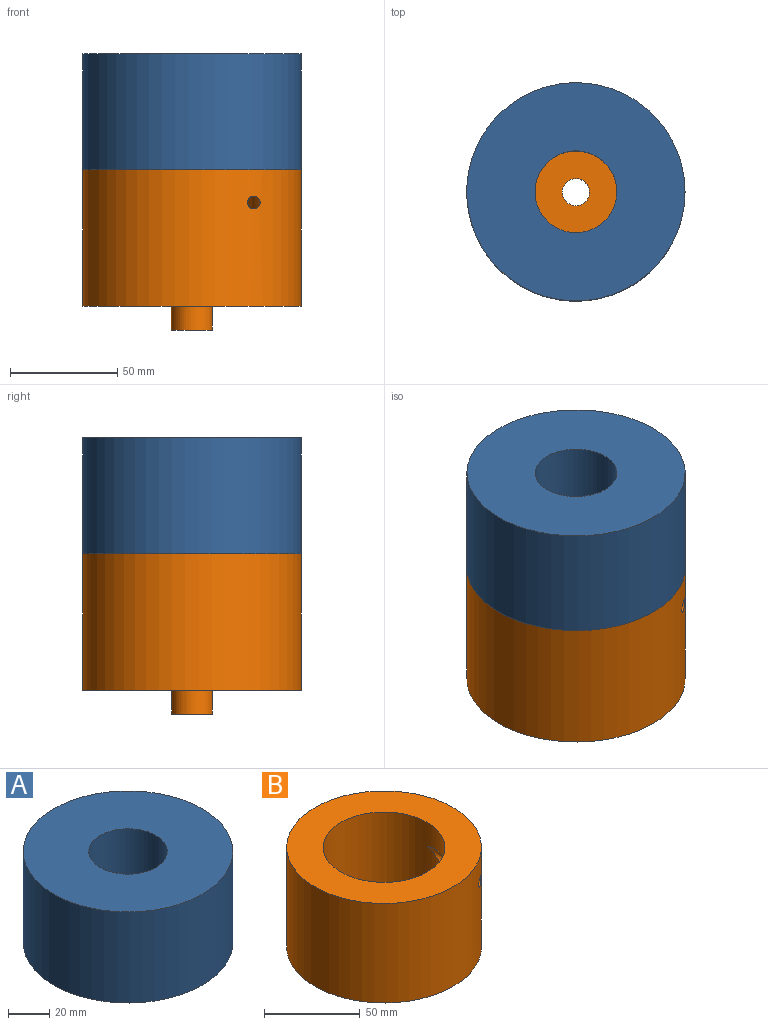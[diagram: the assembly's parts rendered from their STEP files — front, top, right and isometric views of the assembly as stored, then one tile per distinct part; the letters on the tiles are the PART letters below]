
ASSEMBLY  parts=2 mates=1
PART A: 6 faces, bbox 101.6x101.6x65.1 mm
  f0: cylinder r=31.75mm len=63.5mm, axis (0,0,1), area 2219.4mm2, adj f1,f5
  f1: plane 101.6x101.6mm, normal (0,0,-1), area 4940.4mm2, adj f0,f2
  f2: cylinder r=50.8mm len=101.6mm, axis (0,0,1), area 17228.1mm2, adj f1,f3
  f3: plane 101.6x101.6mm, normal (0,0,1), area 6967.2mm2, adj f2,f4
  f4: cylinder r=19.05mm len=65.1mm, axis (0,0,1), area 7792.1mm2, adj f3,f5
  f5: plane 63.5x63.5mm, normal (0,0,-1), area 2026.8mm2, adj f0,f4
PART B: 9 faces, bbox 101.6x101.6x74.6 mm
  f0: cylinder r=31.75mm len=63.5mm, axis (0,0,1), area 10691.1mm2, adj f2,f3,f8
  f1: cylinder r=50.8mm len=101.6mm, axis (0,0,1), area 20236mm2, adj f2,f7,f8
  f2: plane 101.6x101.6mm, normal (0,0,1), area 4940.4mm2, adj f0,f1
  f3: plane 63.5x63.5mm, normal (0,0,1), area 3040.2mm2, adj f0,f4
  f4: cylinder r=6.35mm len=20.65mm, axis (0,0,1), area 823.9mm2, adj f3,f5
  f5: plane 19.05x19.05mm, normal (0,0,-1), area 158.3mm2, adj f4,f6
  f6: cylinder r=9.53mm len=19.05mm, axis (0,0,1), area 665.8mm2, adj f5,f7
  f7: plane 101.6x101.6mm, normal (0,0,-1), area 7822.3mm2, adj f1,f6
  f8: cylinder r=2.92mm len=43.7mm, axis (0,1,0), area 548.3mm2, adj f0,f1
PLACE A t=(0,0,63.5)mm
PLACE B at identity
MATE fastened A.f0 <-> B.f0  axis (0,0,-1) through (0,0,63.5)mm
